# Revit family: 304_c5154dfa51f3457d8d888647143f1f
name_source: partatom
category: Pipe Accessories
revit_build: Autodesk Revit 2017 (Build: 20160225_1515(x64)
units: mm (PartAtom-declared; Revit-internal decimal feet)

## family parameters
Always vertical = Yes
Cut with Voids When Loaded = No
Part Type = Valve - Breaks Into
Round Connector Dimension = Use Diameter
Shared = No
Work Plane-Based = No

## types (6) — shared parameters
CAT0 = Yes
DD4 = 13 mm  [stored 0.0426509 ft]
Description = BALANCING VALVE - VARIABLE ORIFICE - PN 25
F = 25 mm  [stored 0.082021 ft]
HH7 = 19 mm  [stored 0.062336 ft]
HH7__ve = -19 mm  [stored -0.062336 ft]
L2D_Min = 3048 mm
Manufacturer = Cimberio
QmdConnectorList = 301;D;302;D
R11 = 4 mm
R12 = 7 mm  [stored 0.0229659 ft]
magiPartTypeId = 304
magiProductFamilyId = c5154dfa51f3457d8d888647143f1f
zero-valued in all types: MC_Default_elevation

## per-type parameters (varying)
| type | B1 | BB | BB1 | CenSd_R1_6 | D | DD2 | DL | DLL1 | DL__ve | HH1 | HH1__ve | L2D | LL1 | LL2 | R | R1 | RA | W2D | XX | magiProductId |
| Cim 787OT(/2)R(Y) - DN 15 | 54 mm | 83 mm | 27 mm | 11 mm | 15 mm | 6 mm  [stored 0.019685 ft] | 13 mm  [stored 0.0426509 ft] | 11 mm | -13 mm  [stored -0.0426509 ft] | 54 mm | -54 mm | 59 mm | 30 mm  [stored 0.0984252 ft] | 34 mm  [stored 0.111549 ft] | 8 mm  [stored 0.0262467 ft] | 13 mm  [stored 0.0426509 ft] | 45.00° | 15 mm  [stored 0.0492126 ft] | 13 mm  [stored 0.0426509 ft] | dccc15f57ea849c5bf785015298feb |
| Cim 787OT(/2)R(Y) - DN 50 | 70 mm | 105 mm | 35 mm  [stored 0.114829 ft] | 26 mm | 50 mm | 15 mm  [stored 0.0492126 ft] | 19 mm  [stored 0.062336 ft] | 44 mm | -19 mm  [stored -0.062336 ft] | 98 mm | -98 mm | 147 mm | 74 mm | 109 mm | 26 mm | 30 mm  [stored 0.0984252 ft] | 45.00° | 50 mm | 51 mm | 23b5512a7eb34b1b8928fc86ddf105 |
| Cim 787OT(/2)R(Y) - DN 40 | 64 mm | 107 mm | 32 mm  [stored 0.104987 ft] | 22 mm  [stored 0.0721785 ft] | 40 mm | 13 mm  [stored 0.0426509 ft] | 16 mm  [stored 0.0524934 ft] | 39 mm | -16 mm  [stored -0.0524934 ft] | 103 mm | -103 mm | 131 mm | 66 mm | 99 mm | 21 mm  [stored 0.0688976 ft] | 25 mm  [stored 0.082021 ft] | 50.00° | 40 mm  [stored 0.131234 ft] | 46 mm | 2be9c2e53d8d48ae8d648238277b5b |
| Cim 787OT(/2)R(Y) - DN 32 | 65 mm | 87 mm | 33 mm | 18 mm | 32 mm | 10 mm  [stored 0.0328084 ft] | 16 mm  [stored 0.0524934 ft] | 24 mm  [stored 0.0787402 ft] | -16 mm  [stored -0.0524934 ft] | 71 mm | -71 mm | 101 mm | 51 mm | 69 mm | 17 mm  [stored 0.0557743 ft] | 21 mm  [stored 0.0688976 ft] | 50.00° | 32 mm  [stored 0.104987 ft] | 31 mm | 52d2093c2a8545379304395e93a081 |
| Cim 787OT(/2)R(Y) - DN 25 | 60 mm | 83 mm | 30 mm  [stored 0.0984252 ft] | 15 mm  [stored 0.0492126 ft] | 25 mm | 9 mm | 15 mm  [stored 0.0492126 ft] | 22 mm  [stored 0.0721785 ft] | -15 mm | 70 mm | -70 mm | 85 mm | 43 mm | 56 mm | 13 mm  [stored 0.0426509 ft] | 18 mm | 50.00° | 25 mm  [stored 0.082021 ft] | 24 mm  [stored 0.0787402 ft] | f0957a7971944533b50136cf52b5a3 |
| Cim 787OT(/2)R(Y) - DN 20 | 58 mm | 81 mm | 29 mm | 13 mm  [stored 0.0426509 ft] | 20 mm | 7 mm  [stored 0.0229659 ft] | 13 mm  [stored 0.0426509 ft] | 16 mm  [stored 0.0524934 ft] | -13 mm  [stored -0.0426509 ft] | 50 mm | -50 mm | 68 mm | 34 mm  [stored 0.111549 ft] | 43 mm | 11 mm | 15 mm  [stored 0.0492126 ft] | 45.00° | 20 mm  [stored 0.0656168 ft] | 18 mm | f06ff62262384892b818489e74dd78 |

note: column(s) folded — value = type name in every type: magiProductCode

note: [stored X ft] marks values corroborated as IEEE doubles in the binary element streams (Revit-internal decimal feet)

## geometry (parser evidence)
native form markers: Sweep x2
no freeform markers — native parametric forms only
